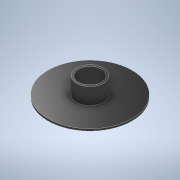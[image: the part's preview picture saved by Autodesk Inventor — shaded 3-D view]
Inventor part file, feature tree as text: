
AUTODESK INVENTOR PART (.ipt)
format: ipt  version: 2021 (Build 250183000, 183)  size: 125,952 bytes
history: native  units: mm
features: revolve x1, thread x1, sketch x1
ambient origin geometry x8: Origin, YZ Plane, XZ Plane, XY Plane, X Axis, Y Axis, Z Axis, Center Point
bodies: Solid1 (feature_tree)
feature tree (3):
  revolve  "Revolution1"  [1 undecoded]
  thread  "Thread1"  [1 undecoded]
  sketch  "Sketch1"  dims[d0=4.0mm d1=8.0mm d2=0.0mm d3=2.5mm d4=3.0mm d7=2.5mm d8=35.0mm d9=13.95mm d10=20.0mm d11=90.0deg d12=8.0mm d13=0.0mm]
note: 2 required parameter values undecoded (feature->parameter linkage not recoverable at this tier; creation-order binding heuristic only, values carry confidence <= 0.55)